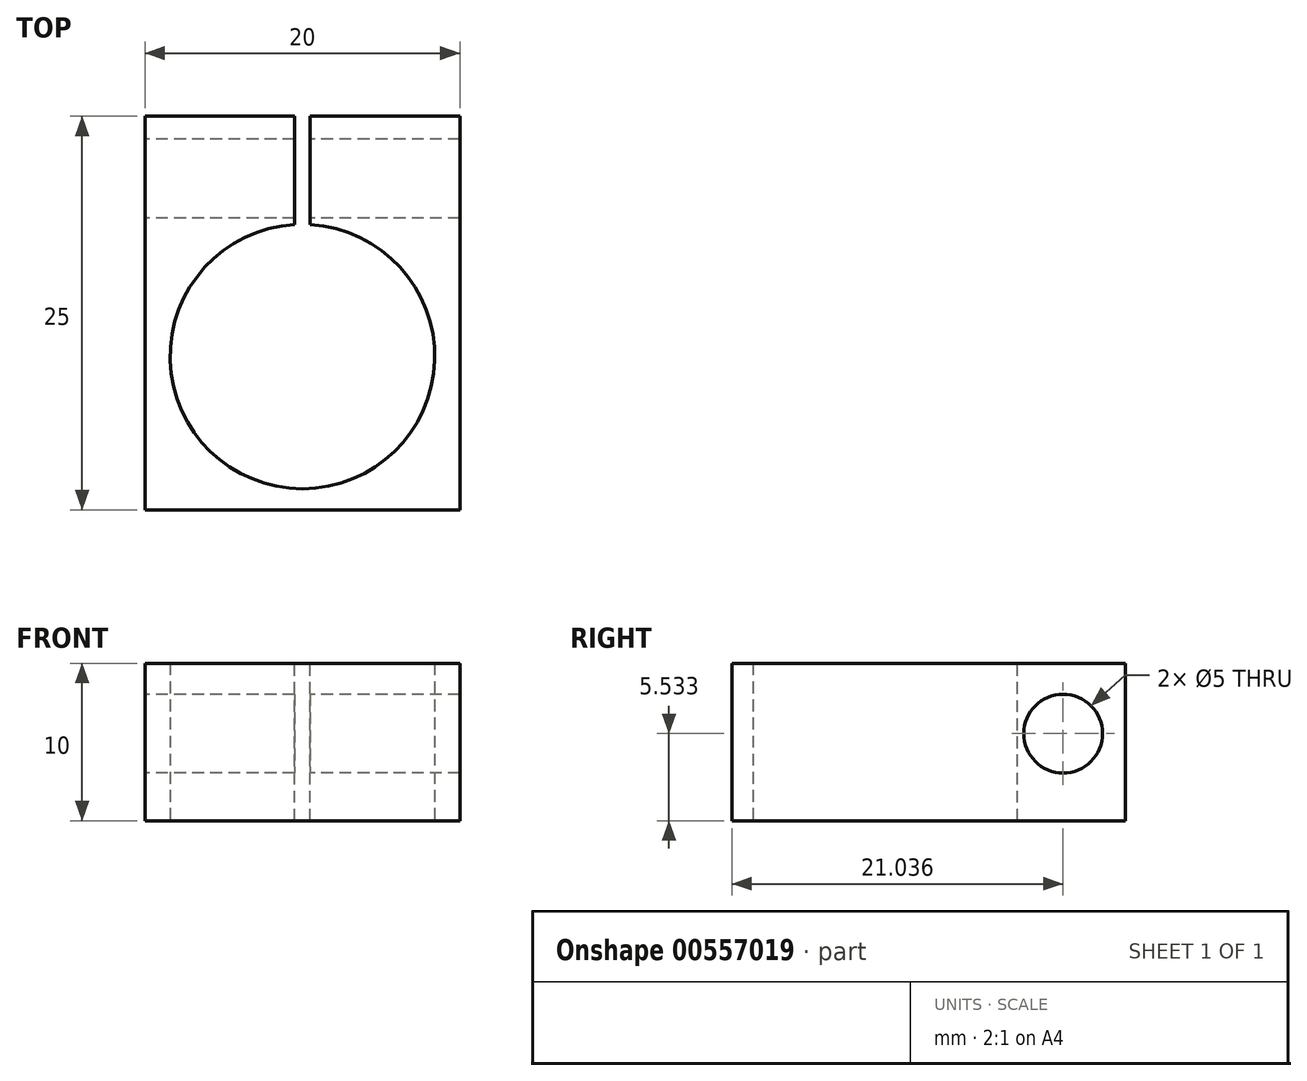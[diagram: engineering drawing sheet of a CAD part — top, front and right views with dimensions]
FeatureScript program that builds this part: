
annotation { "Feature Type Name" : "Feature", "Feature Type Description" : "" }
export const myFeature = defineFeature(function(context is Context, id is Id, definition is map)
    precondition{}
    {
        {
            var Q0;
            Q0=qCreatedBy(makeId("Top.planeOp"),FACE);
            var sketch = newSketch(context, id + "F0", { "sketchPlane" : qUnion([Q0])});
            skLineSegment(sketch, "E0.bottom", {"start": v(10, -12.5) * mm, "end": v(-10, -12.5) * mm});
            skLineSegment(sketch, "E0.top", {"start": v(10, 12.5) * mm, "end": v(-10, 12.5) * mm});
            skLineSegment(sketch, "E0.left", {"start": v(10, -12.5) * mm, "end": v(10, 12.5) * mm});
            skLineSegment(sketch, "E0.right", {"start": v(-10, -12.5) * mm, "end": v(-10, 12.5) * mm});
            skPoint(sketch, "E0.middle", {"position": v(0, 0) * mm});
            skCircle(sketch, "E1", {"center": v(0, -2.76) * mm, "radius": 8.4 * mm});
            skSolve(sketch);
        }
        {
            var Q0;
            Q0=qSketchRegion(id+"F0",true);
            extrude(context, id + "F1", {"entities" : qUnion([Q0]), "depth" : 10 * mm, "offsetDistance" : 25 * mm});
        }
        {
            var Q0;
            Q0=makeQuery(id+"F1.opExtrude","CAP_FACE",FACE,{"disambiguationData":[OSD([sQuery(id+"F0.wireOp",EDGE,"E0.bottom"),sQuery(id+"F0.wireOp",EDGE,"E0.top"),sQuery(id+"F0.wireOp",EDGE,"E0.left"),sQuery(id+"F0.wireOp",EDGE,"E0.right"),sQuery(id+"F0.wireOp",EDGE,"E1")])],"isStart":false});
            var sketch = newSketch(context, id + "F2", { "sketchPlane" : qUnion([Q0])});
            skLineSegment(sketch, "E2.bottom", {"start": v(-0.5, 12.5) * mm, "end": v(0.5, 12.5) * mm});
            skLineSegment(sketch, "E2.top", {"start": v(-0.5, 5.62) * mm, "end": v(0.5, 5.62) * mm});
            skLineSegment(sketch, "E2.left", {"start": v(-0.5, 12.5) * mm, "end": v(-0.5, 5.62) * mm});
            skLineSegment(sketch, "E2.right", {"start": v(0.5, 12.5) * mm, "end": v(0.5, 5.62) * mm});
            skSolve(sketch);
        }
        {
            var Q0;
            Q0=qSketchRegion(id+"F2",true);
            extrude(context, id + "F3", {"entities" : qUnion([Q0]), "operationType" : NewBodyOperationType.REMOVE, "oppositeDirection" : true, "depth" : 10 * mm, "offsetDistance" : 25 * mm});
        }
        {
            var Q0;
            Q0=makeQuery(id+"F1.opExtrude","SWEPT_FACE",FACE,{"disambiguationData":[OSD([sQuery(id+"F0.wireOp",EDGE,"E0.right")])]});
            var sketch = newSketch(context, id + "F4", { "sketchPlane" : qUnion([Q0])});
            skCircle(sketch, "E3", {"center": v(-8.54, 5.53) * mm, "radius": 2.5 * mm});
            skSolve(sketch);
        }
        {
            var Q0;
            Q0=qSketchRegion(id+"F4",true);
            extrude(context, id + "F5", {"entities" : qUnion([Q0]), "operationType" : NewBodyOperationType.REMOVE, "oppositeDirection" : true, "depth" : 20 * mm, "offsetDistance" : 25 * mm});
        }
    });
